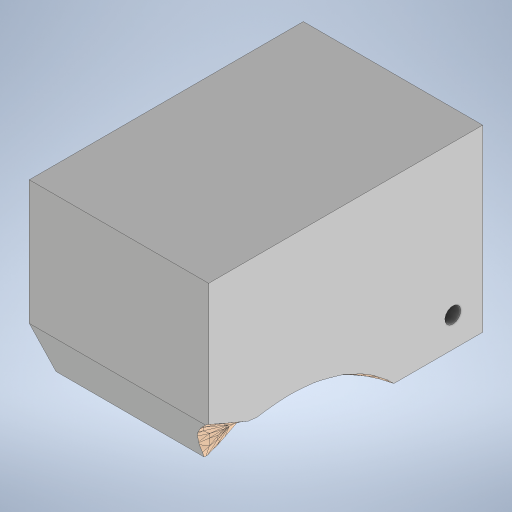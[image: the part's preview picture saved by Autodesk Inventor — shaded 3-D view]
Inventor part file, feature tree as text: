
AUTODESK INVENTOR PART (.ipt)
format: ipt  version: 2024 (Build 280153000, 153)  size: 10,676,224 bytes
history: native  units: mm
features: other x6, sketch x6, extrude x5, plane x2
ambient origin geometry x8: Origin, YZ Plane, XZ Plane, XY Plane, X Axis, Y Axis, Z Axis, Center Point
bodies: Body1 (feature_tree)
feature tree (19):
  other  "M.ipt"
  plane  "Plano de trabajo1"
  extrude  "Extrusión1"  [1 undecoded]
  other  "Combinar1"
  sketch  "Boceto3"  dims[d2=550.0mm d3=520.0mm]
  sketch  "Boceto4"  dims[d4=550.0mm d5=0.0mm d6=129.8482mm]
  plane  "Plano de trabajo2"
  sketch  "Boceto5"  dims[d17=180.0mm d18=180.0mm]
  extrude  "Extrusión2"  Depth=520.0mm
  extrude  "Extrusión3"  Depth=129.8482mm
  extrude  "Extrusión4"  Depth=180.0mm
  extrude  "Extrusión5"  Depth=180.0mm
  other  "Sólido1::M.ipt"
  other  "OperaciónIdentificador1"
  sketch  "Boceto1"  dims[d0=25.0mm d1=-365.0mm]
  other  "Sólido2"
  sketch  "Boceto6"  dims[d22=326.0mm d23=180.0mm]
  sketch  "Boceto7"  dims[d24=180.0mm d25=180.0mm d26=10.0mm d27=0.0mm d28=10.0mm d29=0.0mm d30=30.0mm d31=30.0mm d32=16.0mm d33=16.0mm d34=0.0mm d35=30.0mm d36=30.0mm d37=16.0mm d38=16.0mm d39=0.0mm d14=0.5mm d15=0.872665mm d16=0.5mm d19=0.5mm d20=0.872665mm d21=0.5mm]
  other  "Sólido1"
note: 1 required parameter value undecoded (feature->parameter linkage not recoverable at this tier; creation-order binding heuristic only, values carry confidence <= 0.55)
